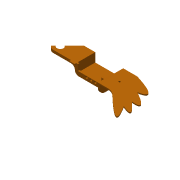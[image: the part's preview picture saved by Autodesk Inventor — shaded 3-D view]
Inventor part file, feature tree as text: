
AUTODESK INVENTOR PART (.ipt)
format: ipt  version: 2016 (Build 200138000, 138)  size: 227,328 bytes
history: native  units: in
note: dims shown in document units (in); Inventor stores cm internally (conversion verified against a paired STEP export)
features: sketch x11, other x3
ambient origin geometry x8: Origin, YZ Plane, XZ Plane, XY Plane, X Axis, Y Axis, Z Axis, Center Point
bodies: Solid1 (feature_tree)
feature tree (14):
  other  "P_ankle02_001.ipt"
  other  "Solid1::P_ankle02_001.ipt"
  other  "TaggingFeature1"
  sketch  "Sketch1"  dims[d0=0.3937in]
  sketch  "Sketch3"
  sketch  "Sketch4"
  sketch  "Sketch5"
  sketch  "Sketch6"
  sketch  "Sketch8"
  sketch  "Sketch7"
  sketch  "Sketch9"
  sketch  "Sketch10"
  sketch  "Sketch11"
  sketch  "Sketch12"
